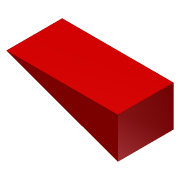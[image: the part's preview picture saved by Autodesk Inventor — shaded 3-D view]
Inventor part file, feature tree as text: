
AUTODESK INVENTOR PART (.ipt)
format: ipt  version: 2012 (Build 160160000, 160)  size: 68,096 bytes
history: native  units: in
note: dims shown in document units (in); Inventor stores cm internally (conversion verified against a paired STEP export)
features: extrude x1, sketch x1
ambient origin geometry x8: Origin, YZ Plane, XZ Plane, XY Plane, X Axis, Y Axis, Z Axis, Center Point
bodies: Solid1 (feature_tree)
feature tree (2):
  extrude  "Extrusion1"  Depth=2.0in
  sketch  "Sketch1"  dims[d0=0.1374in d1=2.0in d2=1.0in d3=0.0in]
